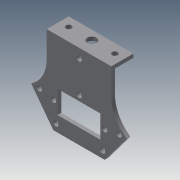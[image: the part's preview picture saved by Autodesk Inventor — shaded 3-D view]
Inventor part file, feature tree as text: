
AUTODESK INVENTOR PART (.ipt)
format: ipt  version: 2013 (Build 170138000, 138)  size: 1,124,352 bytes
history: native  units: mm
features: sketch x103, extrude x90, fillet x2
ambient origin geometry x8: Origin, YZ Plane, XZ Plane, XY Plane, X Axis, Y Axis, Z Axis, Center Point
bodies: Solid1 (feature_tree)
feature tree (195):
  extrude  "Extrusion1"  Depth=10.0mm
  extrude  "Extrusion2"  Depth=10.0mm
  sketch  "Sketch3"  dims[d8=2.0mm d9=0.0mm d11=3.0mm]
  extrude  "Extrusion3"  Depth=3.0mm
  extrude  "Extrusion4"  Depth=3.0mm
  extrude  "Extrusion5"  Depth=10.0mm TaperAngle=0.0deg
  extrude  "Extrusion6"  Depth=3.0mm
  sketch  "Sketch8"  dims[d24=10.0mm d25=0.0mm d26=2.0mm d27=0.0mm]
  extrude  "Extrusion7"  Depth=3.0mm
  extrude  "Extrusion8"  Depth=2.0mm TaperAngle=0.0deg
  extrude  "Extrusion9"  Depth=3.0mm
  extrude  "Extrusion10"  Depth=2.0mm TaperAngle=0.0deg
  extrude  "Extrusion11"  Depth=4.0mm
  extrude  "Extrusion12"  Depth=4.0mm
  extrude  "Extrusion13"  Depth=1.8mm
  sketch  "Sketch16"  dims[d61=4.0mm d62=4.0mm]
  extrude  "Extrusion14"  Depth=4.0mm
  extrude  "Extrusion15"  Depth=12.0mm
  extrude  "Extrusion16"  Depth=4.0mm
  extrude  "Extrusion17"  Depth=16.0mm
  sketch  "Sketch21"  dims[d75=30.0mm d77=2.0mm d78=0.0mm]
  extrude  "Extrusion18"  Depth=10.4mm
  extrude  "Extrusion19"  Depth=4.0mm
  extrude  "Extrusion20"  Depth=20.0mm
  extrude  "Extrusion21"  Depth=2.0mm TaperAngle=0.0deg
  extrude  "Extrusion22"  Depth=2.3mm
  extrude  "Extrusion23"  Depth=24.0mm
  extrude  "Extrusion24"  Depth=2.0mm TaperAngle=0.0deg
  extrude  "Extrusion25"  Depth=3.0mm
  extrude  "Extrusion26"  Depth=2.0mm TaperAngle=0.0deg
  extrude  "Extrusion27"  Depth=2.0mm TaperAngle=0.0deg
  extrude  "Extrusion28"  Depth=4.0mm
  extrude  "Extrusion29"  Depth=3.0mm
  extrude  "Extrusion30"  Depth=3.0mm
  extrude  "Extrusion31"  Depth=3.0mm
  extrude  "Extrusion32"  Depth=4.0mm
  extrude  "Extrusion33"  Depth=3.0mm
  extrude  "Extrusion34"  Depth=2.0mm TaperAngle=0.0deg
  extrude  "Extrusion35"  Depth=2.3mm
  extrude  "Extrusion36"  Depth=4.0mm
  extrude  "Extrusion37"  Depth=2.3mm
  sketch  "Sketch42"  dims[d147=24.0mm d148=24.0mm]
  sketch  "Sketch43"  dims[d149=2.0mm d150=0.0mm d151=2.0mm d152=0.0mm]
  extrude  "Extrusion38"  Depth=2.0mm TaperAngle=0.0deg
  extrude  "Extrusion39"  Depth=2.0mm TaperAngle=0.0deg
  extrude  "Extrusion40"  Depth=20.0mm
  extrude  "Extrusion41"  Depth=20.0mm
  extrude  "Extrusion42"  Depth=24.0mm
  extrude  "Extrusion43"  Depth=2.0mm TaperAngle=0.0deg
  extrude  "Extrusion44"  Depth=3.0mm
  extrude  "Extrusion45"  Depth=20.0mm
  extrude  "Extrusion46"  Depth=2.0mm TaperAngle=0.0deg
  extrude  "Extrusion47"  Depth=3.0mm
  extrude  "Extrusion48"  Depth=3.0mm
  fillet  "Fillet1"  Radius=3.0mm
  extrude  "Extrusion49"  Depth=2.5mm
  fillet  "Fillet2"  Radius=2.0mm
  extrude  "Extrusion50"  Depth=12.5mm
  extrude  "Extrusion51"  Depth=2.5mm
  extrude  "Extrusion52"  Depth=20.0mm
  extrude  "Extrusion53"  Depth=25.0mm
  extrude  "Extrusion54"  Depth=2.0mm TaperAngle=0.0deg
  extrude  "Extrusion55"  Depth=1.5mm
  extrude  "Extrusion56"  Depth=20.0mm
  extrude  "Extrusion57"  Depth=20.0mm
  extrude  "Extrusion58"  Depth=24.0mm
  extrude  "Extrusion59"  Depth=3.4mm
  extrude  "Extrusion60"  Depth=3.0mm
  extrude  "Extrusion61"  Depth=3.0mm
  extrude  "Extrusion62"  Depth=2.0mm TaperAngle=0.0deg
  sketch  "Sketch67"  dims[d218=3.0mm d219=3.0mm]
  extrude  "Extrusion63"  Depth=17.0mm
  extrude  "Extrusion64"  Depth=2.0mm TaperAngle=0.0deg
  extrude  "Extrusion65"  Depth=14.4mm
  sketch  "Sketch71"  dims[d228=1.5mm d229=3.0mm]
  sketch  "Sketch72"  dims[d230=2.0mm d231=0.0mm d233=2.0mm d234=0.0mm]
  extrude  "Extrusion66"  Depth=1.5mm
  sketch  "Sketch73"  dims[d236=14.5mm d237=13.95mm]
  sketch  "Sketch74"  dims[d238=13.95mm d239=3.0mm]
  extrude  "Extrusion67"  Depth=3.0mm
  extrude  "Extrusion68"  Depth=2.0mm TaperAngle=0.0deg
  extrude  "Extrusion69"  Depth=1.5mm
  extrude  "Extrusion70"  Depth=14.4mm
  extrude  "Extrusion71"  Depth=3.0mm
  sketch  "Sketch80"  dims[d256=19.0mm d259=19.0mm]
  sketch  "Sketch81"  dims[d260=2.0mm d261=0.0mm d262=10.0mm]
  extrude  "Extrusion72"  Depth=2.0mm TaperAngle=0.0deg
  extrude  "Extrusion73"  Depth=13.95mm
  sketch  "Sketch84"  dims[d269=2.0mm d270=0.0mm d271=2.0mm d272=0.0mm]
  extrude  "Extrusion74"  Depth=3.0mm
  extrude  "Extrusion75"  Depth=2.0mm TaperAngle=0.0deg
  extrude  "Extrusion76"  Depth=14.4mm
  extrude  "Extrusion77"  Depth=2.0mm
  extrude  "Extrusion78"  Depth=4.0mm
  extrude  "Extrusion79"  Depth=2.0mm TaperAngle=0.0deg
  extrude  "Extrusion80"  Depth=19.0mm
  extrude  "Extrusion81"  Depth=10.0mm
  extrude  "Extrusion82"  Depth=4.0mm
  extrude  "Extrusion83"  Depth=2.0mm TaperAngle=0.0deg
  sketch  "Sketch95"  dims[d298=10.0mm d299=0.0mm]
  extrude  "Extrusion84"  Depth=2.0mm TaperAngle=0.0deg
  extrude  "Extrusion85"  Depth=2.0mm TaperAngle=0.0deg
  extrude  "Extrusion86"  Depth=10.0mm TaperAngle=0.0deg
  extrude  "Extrusion87"  Depth=0.5mm TaperAngle=0.0deg
  sketch  "Sketch100"  dims[d310=16.0mm]
  extrude  "Extrusion88"  Depth=1.5mm TaperAngle=0.0deg
  extrude  "Extrusion89"  Depth=10.4mm
  extrude  "Extrusion90"  Depth=16.0mm
  sketch  "Sketch1"  dims[d2=10.0mm d3=10.0mm]
  sketch  "Sketch2"  dims[d4=10.0mm d7=10.0mm]
  sketch  "Sketch4"  dims[d12=3.0mm d14=3.0mm]
  sketch  "Sketch5"  dims[d15=3.0mm d16=10.0mm d17=0.0mm]
  sketch  "Sketch6"  dims[d20=6.0mm d21=3.0mm]
  sketch  "Sketch7"  dims[d22=6.0mm d23=3.0mm]
  sketch  "Sketch9"  dims[d34=3.0mm d36=3.0mm]
  sketch  "Sketch10"  dims[d37=2.0mm d38=0.0mm d39=2.0mm d40=0.0mm]
  sketch  "Sketch11"  dims[d48=2.0mm d49=4.0mm]
  sketch  "Sketch12"  dims[d51=12.0mm d52=4.0mm]
  sketch  "Sketch13"  dims[d53=2.0mm d54=0.0mm d55=1.8mm]
  sketch  "Sketch14"  dims[d56=2.0mm d57=4.0mm]
  sketch  "Sketch15"  dims[d58=2.0mm d59=0.0mm d60=12.0mm]
  sketch  "Sketch17"  dims[d63=2.0mm d64=0.0mm d65=16.0mm]
  sketch  "Sketch18"  dims[d66=12.0mm d67=10.4mm]
  sketch  "Sketch19"  dims[d68=2.0mm d69=0.0mm d70=4.0mm]
  sketch  "Sketch20"  dims[d71=2.0mm d72=0.0mm d74=20.0mm]
  sketch  "Sketch22"  dims[d83=2.3mm d84=2.3mm]
  sketch  "Sketch23"  dims[d85=2.0mm d86=0.0mm d90=24.0mm]
  sketch  "Sketch24"  dims[d92=24.0mm d93=2.0mm d94=0.0mm]
  sketch  "Sketch25"  dims[d97=3.0mm d98=3.0mm]
  sketch  "Sketch26"  dims[d100=3.0mm d101=2.0mm d102=0.0mm]
  sketch  "Sketch27"  dims[d103=2.0mm d104=0.0mm d105=2.0mm d106=0.0mm]
  sketch  "Sketch28"  dims[d111=4.0mm d112=4.0mm]
  sketch  "Sketch29"  dims[d113=3.0mm d114=3.0mm]
  sketch  "Sketch30"  dims[d116=3.0mm d117=3.0mm]
  sketch  "Sketch31"  dims[d118=3.0mm d119=3.0mm]
  sketch  "Sketch32"  dims[d120=3.0mm d121=4.0mm]
  sketch  "Sketch33"  dims[d122=3.0mm d123=3.0mm]
  sketch  "Sketch34"  dims[d124=3.0mm d125=2.0mm d126=0.0mm]
  sketch  "Sketch35"  dims[d127=2.3mm d128=2.3mm]
  sketch  "Sketch36"  dims[d131=4.0mm d132=4.0mm]
  sketch  "Sketch37"  dims[d133=2.0mm d134=0.0mm d135=2.3mm]
  sketch  "Sketch38"  dims[d136=2.3mm d137=2.0mm d138=0.0mm]
  sketch  "Sketch39"  dims[d139=3.0mm d140=2.0mm d141=0.0mm]
  sketch  "Sketch40"  dims[d142=2.0mm d143=0.0mm d144=20.0mm]
  sketch  "Sketch41"  dims[d145=14.0mm d146=20.0mm]
  sketch  "Sketch44"  dims[d157=3.0mm d158=3.0mm]
  sketch  "Sketch45"  dims[d159=2.0mm d160=0.0mm d161=20.0mm]
  sketch  "Sketch46"  dims[d162=20.0mm d163=2.0mm d164=0.0mm]
  sketch  "Sketch47"  dims[d165=2.0mm d166=0.0mm d167=3.0mm]
  sketch  "Sketch48"  dims[d168=3.0mm d169=3.0mm d170=3.0mm]
  sketch  "Sketch49"  dims[d171=2.5mm d172=2.5mm d173=2.0mm d174=0.0mm]
  sketch  "Sketch50"  dims[d175=2.0mm d176=0.0mm d178=12.5mm]
  sketch  "Sketch51"  dims[d179=12.5mm d180=2.5mm]
  sketch  "Sketch52"  dims[d181=2.5mm d183=20.0mm]
  sketch  "Sketch53"  dims[d185=20.0mm d186=25.0mm]
  sketch  "Sketch54"  dims[d187=25.0mm d188=2.0mm d189=0.0mm]
  sketch  "Sketch55"  dims[d190=1.5mm d191=1.5mm]
  sketch  "Sketch56"  dims[d192=1.5mm d193=20.0mm]
  sketch  "Sketch57"  dims[d194=1.5mm d195=20.0mm]
  sketch  "Sketch58"  dims[d196=24.0mm d197=24.0mm]
  sketch  "Sketch59"  dims[d198=2.0mm d199=0.0mm d200=3.4mm]
  sketch  "Sketch60"  dims[d201=3.4mm d202=3.0mm]
  sketch  "Sketch61"  dims[d203=3.0mm d204=3.0mm]
  sketch  "Sketch62"  dims[d205=3.0mm d206=2.0mm d207=0.0mm]
  sketch  "Sketch63"  dims[d208=2.0mm d209=0.0mm d210=17.0mm]
  sketch  "Sketch64"  dims[d211=14.4mm d212=2.0mm d213=0.0mm]
  sketch  "Sketch65"  dims[d214=19.5mm d215=14.4mm]
  sketch  "Sketch66"  dims[d216=1.5mm d217=1.5mm]
  sketch  "Sketch68"  dims[d220=2.0mm d221=0.0mm d222=2.0mm d223=0.0mm]
  sketch  "Sketch69"  dims[d224=19.5mm d225=1.5mm]
  sketch  "Sketch70"  dims[d226=3.0mm d227=14.4mm]
  sketch  "Sketch75"  dims[d241=3.0mm d242=2.0mm d243=0.0mm]
  sketch  "Sketch76"  dims[d244=2.0mm d245=0.0mm d248=14.4mm]
  sketch  "Sketch77"  dims[d249=21.6mm d250=2.0mm]
  sketch  "Sketch78"  dims[d251=2.0mm d252=4.0mm]
  sketch  "Sketch79"  dims[d253=4.0mm d254=2.0mm d255=0.0mm]
  sketch  "Sketch82"  dims[d263=4.0mm d264=4.0mm]
  sketch  "Sketch83"  dims[d265=2.0mm d266=0.0mm d267=2.0mm d268=0.0mm]
  sketch  "Sketch85"  dims[d273=3.6mm d274=2.0mm d275=0.0mm]
  sketch  "Sketch86"  dims[d276=1.5mm d277=10.0mm d278=0.0mm]
  sketch  "Sketch87"  dims[d279=2.0mm d280=0.5mm d281=0.0mm]
  sketch  "Sketch88"  dims[d282=0.5mm d283=1.5mm d284=0.0mm]
  sketch  "Sketch89"  dims[d285=1.5mm d286=0.0mm d287=10.4mm]
  sketch  "Sketch90"  dims[d288=14.398895mm d289=16.0mm]
  sketch  "Sketch91"  dims[d290=1.5mm d291=0.0mm]
  sketch  "Sketch92"  dims[d292=1.5mm d293=0.0mm]
  sketch  "Sketch93"  dims[d294=10.0mm d295=0.0mm]
  sketch  "Sketch94"  dims[d296=10.0mm d297=0.0mm]
  sketch  "Sketch96"  dims[d300=20.0mm d301=0.0mm]
  sketch  "Sketch97"  dims[d306=1.5mm d307=0.0mm]
  sketch  "Sketch98"  dims[d308=4.0mm]
  sketch  "Sketch99"  dims[d309=7.0mm]
  sketch  "Sketch101"  dims[d311=3.0mm]
  sketch  "Sketch102"  dims[d312=7.0mm]
  sketch  "Sketch103"  dims[d313=16.0mm d314=1.5mm d315=0.0mm d316=5.0mm d317=1.5mm d318=0.0mm d319=1.5mm d320=10.0mm d321=0.0mm d322=7.0mm d323=7.0mm d324=4.0mm d325=7.0mm d326=4.0mm d327=7.0mm d328=4.0mm d329=1.5mm d330=0.0mm d331=4.0mm d332=4.129mm d333=7.0mm d335=3.072mm d336=7.0mm d337=15.0mm d338=1.5mm d339=0.0mm d341=1.5mm d342=0.0mm d343=0.5mm d344=7.0mm d345=18.0mm d346=7.0mm d347=1.5mm d348=0.0mm d349=7.0mm d351=7.0mm d353=1.5mm d354=0.0mm d359=8.3mm d360=11.6mm d361=23.6mm d362=12.4mm d363=1.5mm d364=0.0mm d365=27.9mm d366=0.4mm d367=1.5mm d368=0.0mm d370=0.3mm d371=0.3mm d372=1.5mm d373=0.0mm d374=5.0mm d375=5.0mm d376=1.5mm d377=0.0mm d378=6.3mm d379=12.6mm d380=3.0mm d381=3.0mm d382=1.5mm d383=0.0mm d391=1.5mm d392=0.0mm d395=7.0mm d396=19.0mm d399=7.0mm d400=1.5mm d401=0.0mm d403=1.5mm d404=0.0mm d406=1.5mm d407=3.0mm d409=1.5mm d410=3.0mm d411=1.5mm d412=0.0mm d413=14.5mm d414=3.0mm d415=1.5mm d416=0.0mm d417=3.0mm d418=1.5mm d419=3.0mm d420=2.0mm d421=3.0mm d422=3.0mm d423=1.5mm d424=0.0mm d425=1.5mm d426=1.5mm d427=0.0mm d428=1.5mm d429=1.5mm d430=0.0mm d431=1.5mm d432=0.0mm d433=3.0mm d434=3.0mm d435=3.0mm d436=3.0mm d437=1.5mm d438=0.0mm d439=1.5mm d440=0.0mm d441=3.0mm d442=3.0mm d443=1.5mm d444=0.0mm d445=0.5mm d446=0.0mm d447=0.5mm d448=0.0mm d449=5.0mm d450=5.0mm d451=3.0mm d452=3.0mm d453=2.0mm d454=0.0mm d455=2.0mm d456=2.0mm d457=2.0mm d458=0.0mm d459=2.0mm d460=0.0mm d461=2.0mm d462=0.0mm d464=3.0mm d465=3.0mm d466=2.0mm d467=0.0mm]
